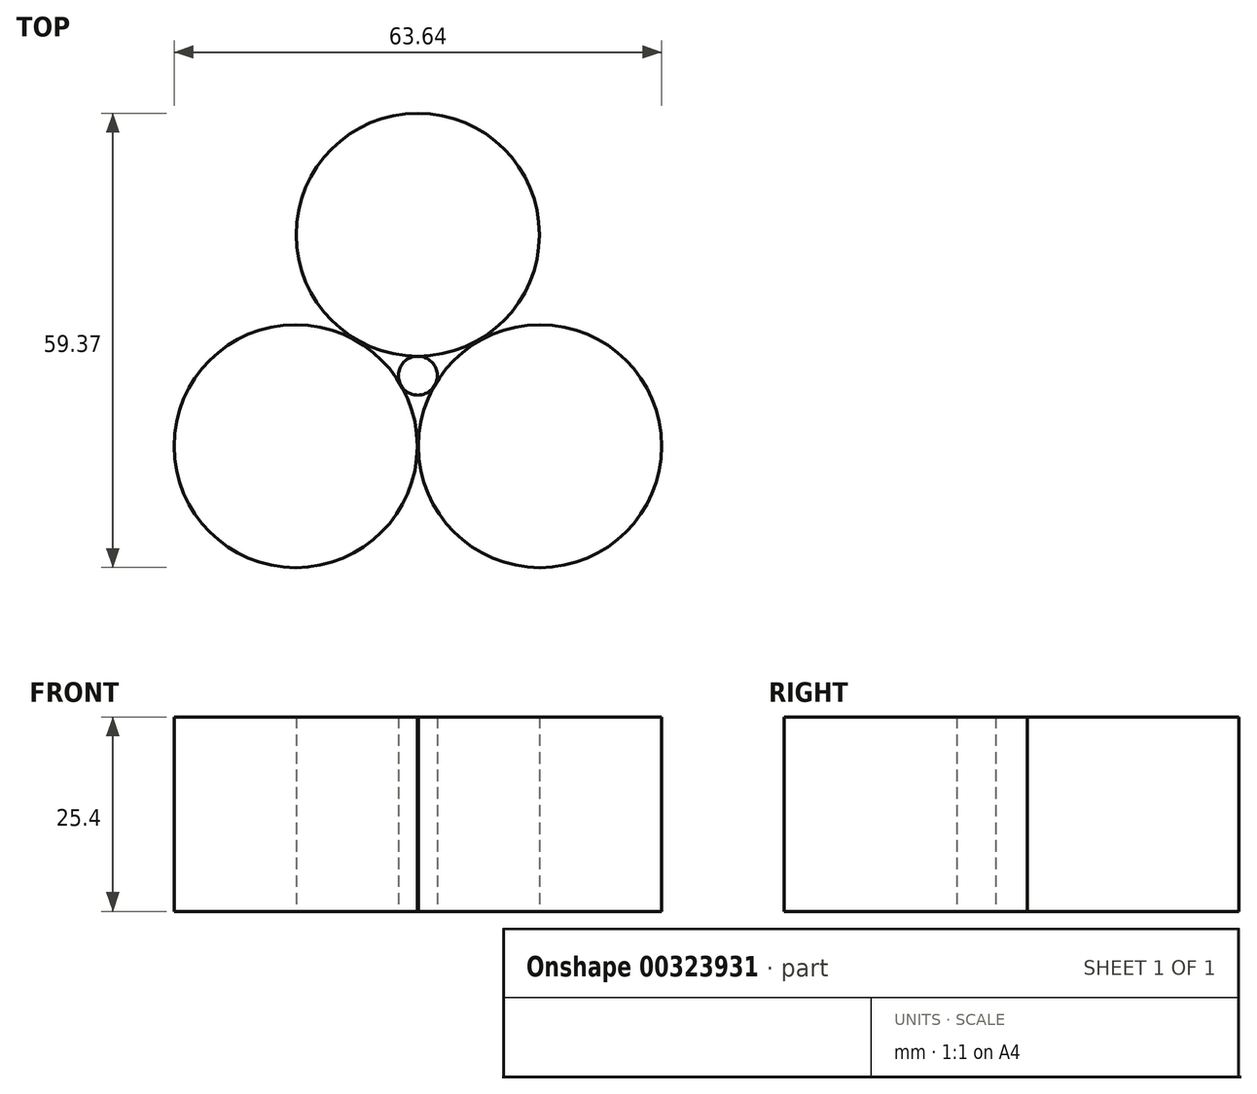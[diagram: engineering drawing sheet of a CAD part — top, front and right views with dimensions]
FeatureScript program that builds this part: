
annotation { "Feature Type Name" : "Feature", "Feature Type Description" : "" }
export const myFeature = defineFeature(function(context is Context, id is Id, definition is map)
    precondition{}
    {
        {
            var Q0;
            Q0=qCreatedBy(makeId("Top.planeOp"),FACE);
            var sketch = newSketch(context, id + "F0", { "sketchPlane" : qUnion([Q0])});
            skCircle(sketch, "E0", {"center": v(0, 0) * mm, "radius": 2.54 * mm});
            skCircle(sketch, "E1", {"center": v(0, 18.41) * mm, "radius": 15.88 * mm});
            skSolve(sketch);
        }
        {
            var Q0;
            Q0=makeQuery(id+"F0.imprint","IMPRINT",FACE,{"disambiguationData":[TD([[makeQuery(id+"F0.imprint","IMPRINT",EDGE,{"derivedFrom":sQuery(id+"F0.wireOp",EDGE,"E1")}),1.0]])]});
            extrude(context, id + "F1", {"entities" : qUnion([Q0]), "depth" : 25.4 * mm});
        }
        {
            var Q0;
            Q0 = qSketchRegion(id + "F0", true);
            extrude(context, id + "F2", {"entities" : qUnion([Q0]), "operationType" : NewBodyOperationType.ADD, "depth" : 25.4 * mm});
        }
        {
            var Q0;
            Q0=makeQuery(id+"F1.opExtrude","SWEPT_BODY",BODY,{"disambiguationData":[OSD([sQuery(id+"F0.wireOp",EDGE,"E1")])]});
            var Q1;
            Q1=makeQuery(id+"F2.opExtrude","SWEPT_FACE",FACE,{"disambiguationData":[OSD([sQuery(id+"F0.wireOp",EDGE,"E0")])]});
            circularPattern(context, id + "F3", {"entities" : qUnion([Q0]), "axis" : qUnion([Q1]), "angle" : 360 * degree, "instanceCount" : 3, "equalSpace" : true});
        }
    });
